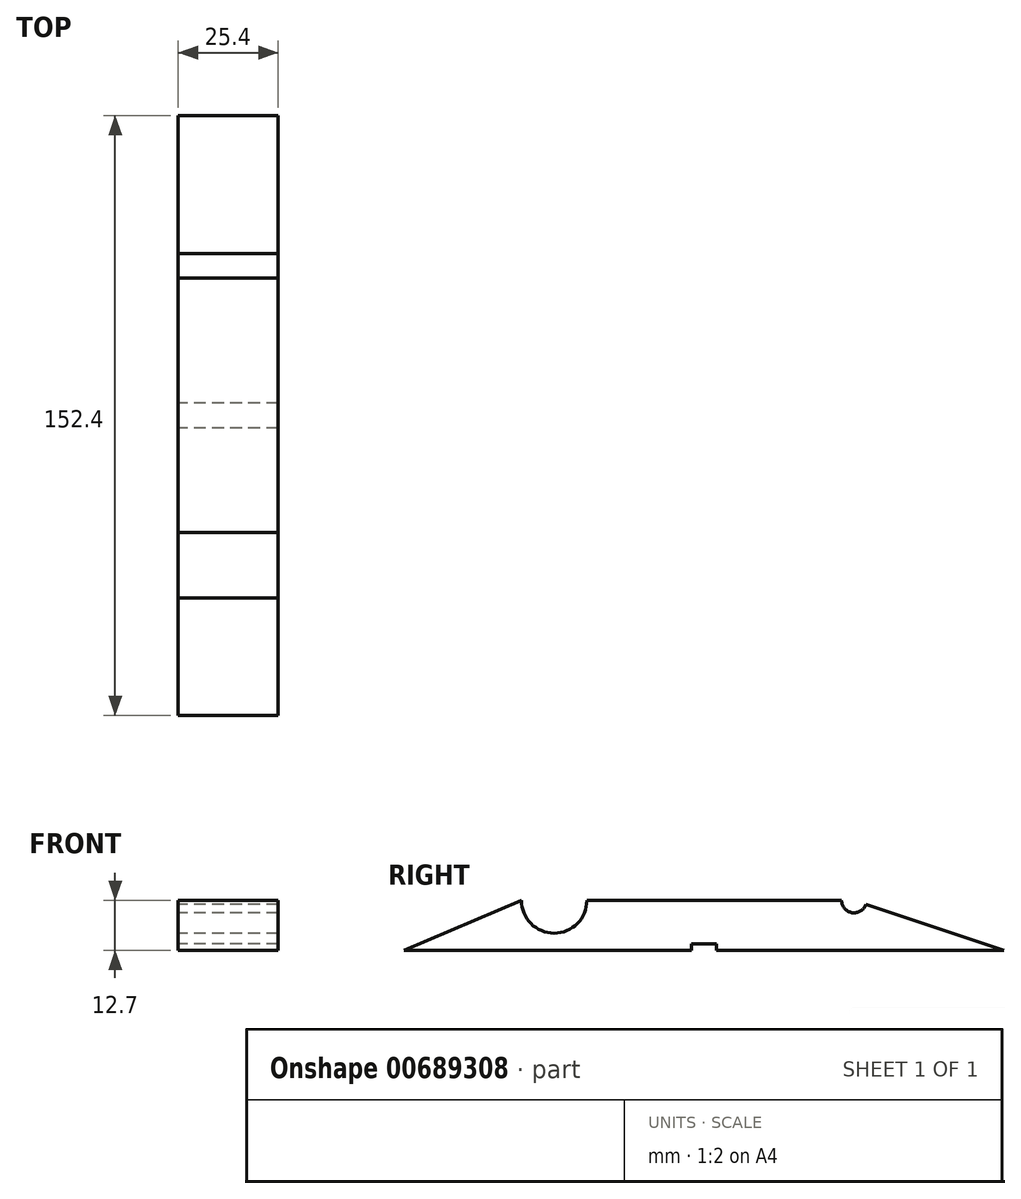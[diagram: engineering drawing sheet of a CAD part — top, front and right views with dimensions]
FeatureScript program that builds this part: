
annotation { "Feature Type Name" : "Feature", "Feature Type Description" : "" }
export const myFeature = defineFeature(function(context is Context, id is Id, definition is map)
    precondition{}
    {
        {
            var Q0;
            Q0=qCreatedBy(makeId("Right.planeOp"),FACE);
            var sketch = newSketch(context, id + "F0", { "sketchPlane" : qUnion([Q0])});
            skLineSegment(sketch, "E0.bottom", {"start": v(34.93, 6.35) * mm, "end": v(3.17, 6.35) * mm});
            skLineSegment(sketch, "E0.top", {"start": v(76.2, -6.35) * mm, "end": v(-76.2, -6.35) * mm});
            skPoint(sketch, "E0.middle", {"position": v(0, 0) * mm});
            skArc(sketch, "E1", {"start": v(-46.43, 6.35) * mm, "mid": v(-38.1, -1.98) * mm, "end": v(-29.77, 6.35) * mm});
            skLineSegment(sketch, "E2", {"start": v(0, 0) * mm, "end": v(0, -6.35) * mm});
            skPoint(sketch, "E3.middle", {"position": v(0, 6.35) * mm});
            skLineSegment(sketch, "E4.bottom", {"start": v(3.18, -4.76) * mm, "end": v(-3.17, -4.76) * mm});
            skLineSegment(sketch, "E4.left", {"start": v(3.18, -4.76) * mm, "end": v(3.18, -6.35) * mm});
            skLineSegment(sketch, "E4.right", {"start": v(-3.17, -4.76) * mm, "end": v(-3.17, -6.35) * mm});
            skPoint(sketch, "E4.middle", {"position": v(0, -6.35) * mm});
            skLineSegment(sketch, "E5.trimOffspring", {"start": v(-3.18, 6.35) * mm, "end": v(-29.77, 6.35) * mm});
            skPoint(sketch, "E6.orphan", {"position": v(-3.18, 7.94) * mm});
            skPoint(sketch, "E7.orphan", {"position": v(3.17, 7.94) * mm});
            skPoint(sketch, "E4.top.end.orphan", {"position": v(-3.18, -7.94) * mm});
            skPoint(sketch, "E8.orphan", {"position": v(3.18, -7.94) * mm});
            skPoint(sketch, "E9.end.orphan", {"position": v(38.1, 6.35) * mm});
            skLineSegment(sketch, "E10", {"start": v(-46.43, 6.35) * mm, "end": v(-76.2, -6.35) * mm});
            skPoint(sketch, "E0.right.start.orphan", {"position": v(-76.2, 6.35) * mm});
            skArc(sketch, "E11", {"start": v(34.93, 6.35) * mm, "mid": v(37.6, 3.22) * mm, "end": v(41.11, 5.35) * mm});
            skPoint(sketch, "E12.center.orphan", {"position": v(38.1, 0) * mm});
            skPoint(sketch, "E13.orphan", {"position": v(76.2, 6.35) * mm});
            skLineSegment(sketch, "E14", {"start": v(41.11, 5.35) * mm, "end": v(76.2, -6.35) * mm});
            skLineSegment(sketch, "E15", {"start": v(-3.18, 6.35) * mm, "end": v(3.17, 6.35) * mm});
            skPoint(sketch, "E16.orphan", {"position": v(-3.18, 4.76) * mm});
            skPoint(sketch, "E3.left.end.orphan", {"position": v(3.17, 4.76) * mm});
            skSolve(sketch);
        }
        {
            var Q0;
            Q0=makeQuery(id+"F0.imprint","IMPRINT",FACE,{"disambiguationData":[TD([[makeQuery(id+"F0.imprint","IMPRINT",EDGE,{"derivedFrom":sQuery(id+"F0.wireOp",EDGE,"E1")}),-1.0]])]});
            var Q1;
            {var subQ1=sQuery(id+"F0.wireOp",EDGE,"cPk64hCO-RSHn-0skk-BxEM-qDqAWIykB7Ow");Q1=makeQuery(id+"F0.imprint","IMPRINT",FACE,{"disambiguationData":[TD([[makeQuery(id+"F0.imprint","IMPRINT",EDGE,{"derivedFrom":subQ1}),-1.0]])]});}
            var Q2;
            Q2=makeQuery(id+"F0.imprint","IMPRINT",FACE,{"disambiguationData":[TD([[makeQuery(id+"F0.imprint","IMPRINT",EDGE,{"derivedFrom":sQuery(id+"F0.wireOp",EDGE,"E0.bottom")}),1.0]])]});
            extrude(context, id + "F1", {"entities" : qUnion([Q0, Q1, Q2]), "depth" : 25.4 * mm, "offsetDistance" : 25.4 * mm});
        }
    });
